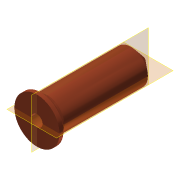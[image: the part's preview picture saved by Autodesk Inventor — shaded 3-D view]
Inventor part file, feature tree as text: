
AUTODESK INVENTOR PART (.ipt)
format: ipt  version: 2014 (Build 180170000, 170)  size: 157,184 bytes
history: native  units: mm
features: sketch x5, extrude x3, revolve x2, chamfer x1
ambient origin geometry x8: Origin, YZ Plane, XZ Plane, XY Plane, X Axis, Y Axis, Z Axis, Center Point
bodies: Solid1 (feature_tree)
feature tree (11):
  extrude  "Extrusion1"  Depth=1.0mm TaperAngle=0.0deg
  extrude  "Extrusion2"  Depth=15.668mm TaperAngle=0.0deg
  extrude  "Extrusion3"  Depth=21.0mm TaperAngle=0.0deg
  revolve  "Revolution1"  [1 undecoded]
  revolve  "Revolution2"  Angle=90.0deg
  chamfer  "Chamfer1"  Distance=0.7mm
  sketch  "Sketch1"  dims[d0=8.0mm d1=1.0mm d2=0.0mm]
  sketch  "Sketch2"  dims[d3=6.0mm d4=15.668mm d5=0.0mm]
  sketch  "Sketch3"  dims[d6=2.0mm d7=21.0mm d8=0.0mm]
  sketch  "Sketch4"  dims[d9=6.981317mm d10=0.2mm]
  sketch  "Sketch5"  dims[d11=30.0deg d13=90.0deg d14=0.7mm d15=90.0deg d16=0.3mm d17=2.0mm d18=45.0deg d19=45.0deg d20=0.05mm d21=0.4mm d22=0.05mm]
note: 1 required parameter value undecoded (feature->parameter linkage not recoverable at this tier; creation-order binding heuristic only, values carry confidence <= 0.55)
